# Revit family: EKF_EE_ПланкаПНЩРМ_PROxima
name_source: partatom
category: Электрооборудование
units: mm (PartAtom-declared; Revit-internal decimal feet)

## family parameters
Всегда вертикально = Нет
На основе рабочей плоскости = Да
Общий = Да
При загрузке вырезать с полостями = Нет
Размер круглого соединителя = Использовать диаметр
Тип детали = Силовой щит
Точка расчета площади = Нет

## types (2) — shared parameters
ADSK_Единица измерения = шт.
ADSK_Завод-изготовитель = EKF
ADSK_Количество = 1
ADSK_Марка = Планка
ADSK_Материал = Сталь_Оцинкованная
ADSK_Обозначение = Планка
ADSK_Размер_Высота = 30 мм
ADSK_Размер_Глубина = 10 мм
t = 1.2 мм
Изготовитель = EKF
Серия номенклатуры = Unit PROxima
Степень защиты IP = -
ТВ = EKF_2
Тип установки = -
Шаг = 30 мм
zero-valued in all types: ADSK_Масса, Отметка по умолчанию

## per-type parameters (varying)
| type | ADSK_Код изделия | ADSK_Наименование | ADSK_Размер_Ширина | Отступ | Тип |
| Планка 30x545мм (ЩРНМ-8, ЩРНМ-9) | po-30x545 | Планка 30x545мм (ЩРНМ-8 ЩРНМ-9) | 545 мм | 47.5 мм | 140 мм |
| Планка 30x745мм (ЩРНМ-8L, ЩРНМ-9L) | po-30x745 | Планка 30x745мм (ЩРНМ-8L ЩРНМ-9L) | 745 мм | 57.5 мм | 141 мм |
